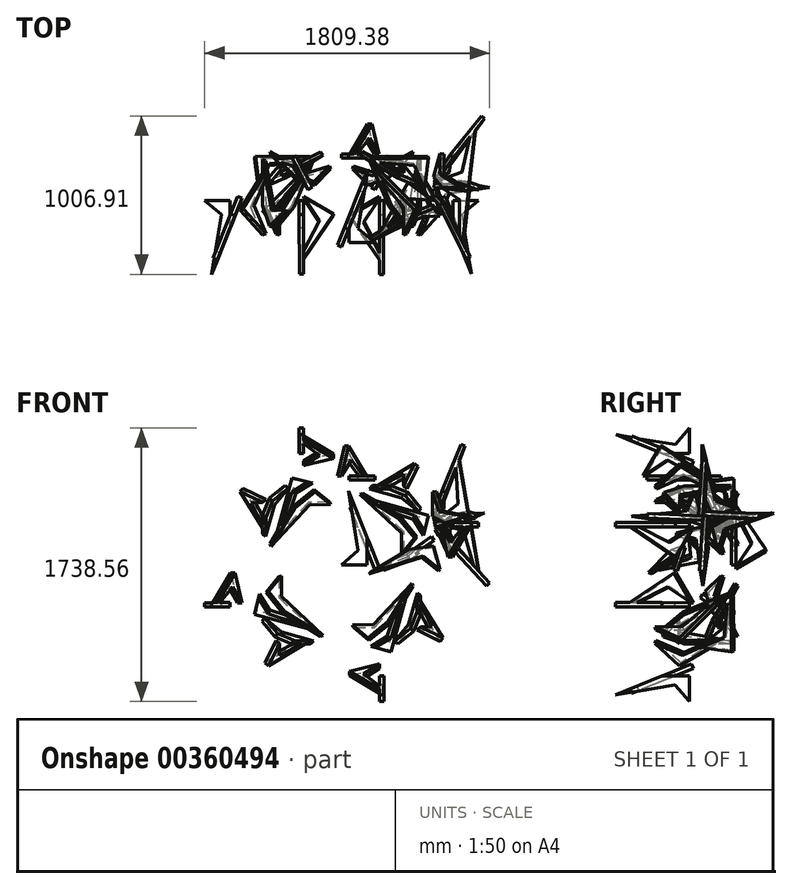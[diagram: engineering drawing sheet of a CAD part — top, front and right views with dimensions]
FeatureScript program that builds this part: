
annotation { "Feature Type Name" : "Feature", "Feature Type Description" : "" }
export const myFeature = defineFeature(function(context is Context, id is Id, definition is map)
    precondition{}
    {
        {
            var Q0;
            Q0=qCreatedBy(makeId("Top.planeOp"),FACE);
            var sketch = newSketch(context, id + "F0", { "sketchPlane" : qUnion([Q0])});
            skLineSegment(sketch, "E0", {"start": v(-57.1, -50.24) * mm, "end": v(-57.1, -222.83) * mm});
            skLineSegment(sketch, "E1", {"start": v(-57.1, -222.83) * mm, "end": v(105.7, -222.83) * mm});
            skLineSegment(sketch, "E2", {"start": v(105.7, -222.83) * mm, "end": v(0, -132.78) * mm});
            skLineSegment(sketch, "E3", {"start": v(0, -132.78) * mm, "end": v(61.93, 245.54) * mm});
            skLineSegment(sketch, "E4", {"start": v(61.93, 245.54) * mm, "end": v(-57.1, -50.24) * mm});
            skSolve(sketch);
        }
        {
            var Q0;
            Q0=makeQuery(id+"F0.imprint","IMPRINT",FACE,{"disambiguationData":[TD([[makeQuery(id+"F0.imprint","IMPRINT",EDGE,{"derivedFrom":sQuery(id+"F0.wireOp",EDGE,"E0")}),1.0]])]});
            extrude(context, id + "F1", {"entities" : qUnion([Q0]), "oppositeDirection" : true, "depth" : 27.38 * mm});
        }
        {
            var Q0;
            Q0=makeQuery(id+"F1.opExtrude","SWEPT_FACE",FACE,{"disambiguationData":[OSD([sQuery(id+"F0.wireOp",EDGE,"E4")])]});
            var sketch = newSketch(context, id + "F2", { "sketchPlane" : qUnion([Q0])});
            skLineSegment(sketch, "E5", {"start": v(-307.56, -97.86) * mm, "end": v(149.71, 190.27) * mm});
            skLineSegment(sketch, "E6", {"start": v(149.71, 190.27) * mm, "end": v(269.6, 0) * mm});
            skLineSegment(sketch, "E7", {"start": v(269.6, 0) * mm, "end": v(104.64, 99.82) * mm});
            skLineSegment(sketch, "E8", {"start": v(104.64, 99.82) * mm, "end": v(-307.56, -97.86) * mm});
            skSolve(sketch);
        }
        {
            var Q0;
            {var subQ4=sQuery(id+"F2.wireOp",EDGE,"E6");Q0=makeQuery(id+"F2.imprint","IMPRINT",FACE,{"disambiguationData":[TD([[makeQuery(id+"F2.imprint","IMPRINT",EDGE,{"derivedFrom":subQ4}),-1.0]])]});}
            extrude(context, id + "F3", {"entities" : qUnion([Q0]), "operationType" : NewBodyOperationType.ADD, "oppositeDirection" : true, "depth" : 30.02 * mm});
        }
        {
            var Q0;
            Q0=qCreatedBy(makeId("Right.planeOp"),FACE);
            var sketch = newSketch(context, id + "F4", { "sketchPlane" : qUnion([Q0])});
            skLineSegment(sketch, "E9", {"start": v(342.03, 0) * mm, "end": v(80.6, -261.15) * mm});
            skSolve(sketch);
        }
        {
            var Q0;
            Q0=makeQuery(id+"F1.opExtrude","SWEPT_BODY",BODY,{"disambiguationData":[OSD([sQuery(id+"F0.wireOp",EDGE,"E0"),sQuery(id+"F0.wireOp",EDGE,"E1"),sQuery(id+"F0.wireOp",EDGE,"E2"),sQuery(id+"F0.wireOp",EDGE,"E3"),sQuery(id+"F0.wireOp",EDGE,"E4")])]});
            var Q1;
            Q1=sQuery(id+"F4.wireOp",EDGE,"E9");
            circularPattern(context, id + "F5", {"entities" : qUnion([Q0]), "axis" : qUnion([Q1]), "angle" : 180 * degree, "instanceCount" : 4, "oppositeDirection" : true, "equalSpace" : true});
        }
        {
            var Q0;
            Q0=makeQuery(id+"F5.opPattern","COPY",BODY,{"derivedFrom":makeQuery(id+"F1.opExtrude","SWEPT_BODY",BODY,{"disambiguationData":[OSD([sQuery(id+"F0.wireOp",EDGE,"E0"),sQuery(id+"F0.wireOp",EDGE,"E1"),sQuery(id+"F0.wireOp",EDGE,"E2"),sQuery(id+"F0.wireOp",EDGE,"E3"),sQuery(id+"F0.wireOp",EDGE,"E4")])]}),"instanceName":"2"});
            var Q1;
            Q1=makeQuery(id+"F5.opPattern","COPY",EDGE,{"derivedFrom":makeQuery(id+"F1.opExtrude","CAP_EDGE",EDGE,{"disambiguationData":[OSD([sQuery(id+"F0.wireOp",EDGE,"E1")])],"isStart":false}),"instanceName":"1"});
            circularPattern(context, id + "F6", {"entities" : qUnion([Q0]), "axis" : qUnion([Q1]), "angle" : 360 * degree, "instanceCount" : 4, "equalSpace" : true});
        }
        {
            var Q0;
            Q0=makeQuery(id+"F5.opPattern","COPY",BODY,{"derivedFrom":makeQuery(id+"F1.opExtrude","SWEPT_BODY",BODY,{"disambiguationData":[OSD([sQuery(id+"F0.wireOp",EDGE,"E0"),sQuery(id+"F0.wireOp",EDGE,"E1"),sQuery(id+"F0.wireOp",EDGE,"E2"),sQuery(id+"F0.wireOp",EDGE,"E3"),sQuery(id+"F0.wireOp",EDGE,"E4")])]}),"instanceName":"1"});
            var Q1;
            Q1=makeQuery(id+"F6.opPattern","COPY",BODY,{"derivedFrom":makeQuery(id+"F5.opPattern","COPY",BODY,{"derivedFrom":makeQuery(id+"F1.opExtrude","SWEPT_BODY",BODY,{"disambiguationData":[OSD([sQuery(id+"F0.wireOp",EDGE,"E0"),sQuery(id+"F0.wireOp",EDGE,"E1"),sQuery(id+"F0.wireOp",EDGE,"E2"),sQuery(id+"F0.wireOp",EDGE,"E3"),sQuery(id+"F0.wireOp",EDGE,"E4")])]}),"instanceName":"2"}),"instanceName":"2"});
            var Q2;
            Q2=makeQuery(id+"F5.opPattern","COPY",BODY,{"derivedFrom":makeQuery(id+"F1.opExtrude","SWEPT_BODY",BODY,{"disambiguationData":[OSD([sQuery(id+"F0.wireOp",EDGE,"E0"),sQuery(id+"F0.wireOp",EDGE,"E1"),sQuery(id+"F0.wireOp",EDGE,"E2"),sQuery(id+"F0.wireOp",EDGE,"E3"),sQuery(id+"F0.wireOp",EDGE,"E4")])]}),"instanceName":"2"});
            var Q3;
            Q3=makeQuery(id+"F5.opPattern","COPY",EDGE,{"derivedFrom":makeQuery(id+"F1.opExtrude","SWEPT_EDGE",EDGE,{"disambiguationData":[OSD([sQuery(id+"F0.wireOp",EDGE,"E1"),sQuery(id+"F0.wireOp",EDGE,"E2")])]}),"instanceName":"3"});
            circularPattern(context, id + "F7", {"entities" : qUnion([Q0, Q1, Q2]), "axis" : qUnion([Q3]), "angle" : 360 * degree, "instanceCount" : 4, "equalSpace" : true});
        }
        {
            var Q0;
            Q0=makeQuery(id+"F6.opPattern","COPY",BODY,{"derivedFrom":makeQuery(id+"F5.opPattern","COPY",BODY,{"derivedFrom":makeQuery(id+"F1.opExtrude","SWEPT_BODY",BODY,{"disambiguationData":[OSD([sQuery(id+"F0.wireOp",EDGE,"E0"),sQuery(id+"F0.wireOp",EDGE,"E1"),sQuery(id+"F0.wireOp",EDGE,"E2"),sQuery(id+"F0.wireOp",EDGE,"E3"),sQuery(id+"F0.wireOp",EDGE,"E4")])]}),"instanceName":"2"}),"instanceName":"1"});
            var Q1;
            Q1=makeQuery(id+"F6.opPattern","COPY",EDGE,{"derivedFrom":makeQuery(id+"F5.opPattern","COPY",EDGE,{"derivedFrom":makeQuery(id+"F3.opExtrude","CAP_EDGE",EDGE,{"disambiguationData":[OSD([sQuery(id+"F2.wireOp",EDGE,"E6")])],"isStart":false}),"instanceName":"2"}),"instanceName":"1"});
            circularPattern(context, id + "F8", {"entities" : qUnion([Q0]), "axis" : qUnion([Q1]), "angle" : 360 * degree, "instanceCount" : 4, "equalSpace" : true});
        }
    });
